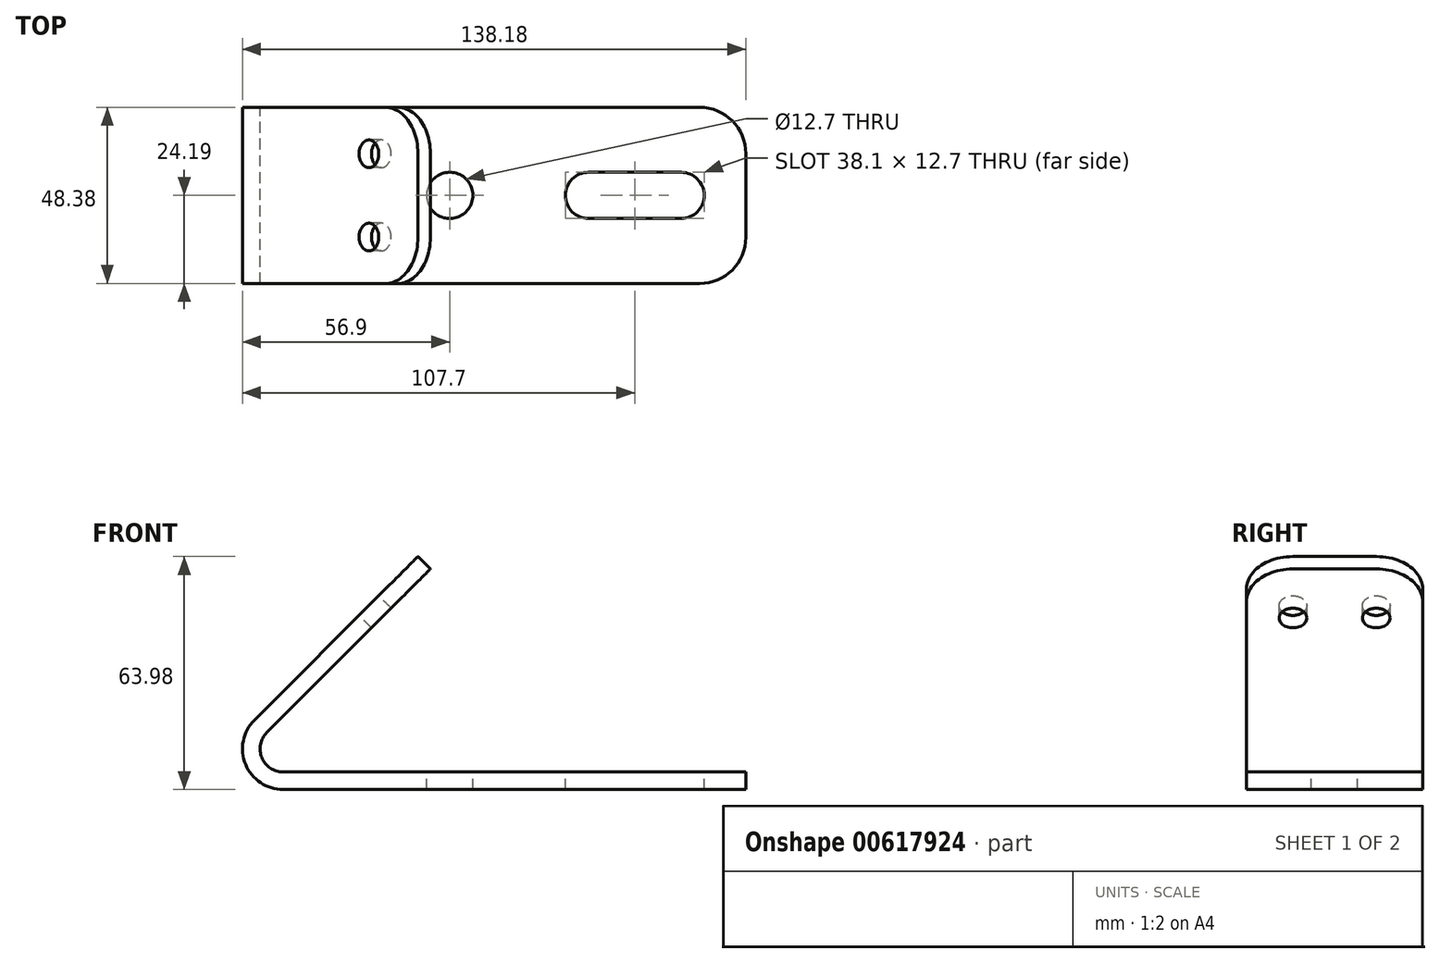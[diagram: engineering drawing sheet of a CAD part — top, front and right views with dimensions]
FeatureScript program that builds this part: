
annotation { "Feature Type Name" : "Feature", "Feature Type Description" : "" }
export const myFeature = defineFeature(function(context is Context, id is Id, definition is map)
    precondition{}
    {
        {
            var Q0;
            Q0=qCreatedBy(makeId("Front.planeOp"),FACE);
            var sketch = newSketch(context, id + "F0", { "sketchPlane" : qUnion([Q0])});
            skLineSegment(sketch, "E0", {"start": v(-8.72, 63.98) * mm, "end": v(-53.62, 19.08) * mm});
            skLineSegment(sketch, "E1", {"start": v(-45.72, 0) * mm, "end": v(81.28, 0) * mm});
            skLineSegment(sketch, "E2", {"start": v(81.28, 0) * mm, "end": v(81.28, 4.83) * mm});
            skLineSegment(sketch, "E3", {"start": v(81.28, 4.83) * mm, "end": v(-45.72, 4.83) * mm});
            skLineSegment(sketch, "E4", {"start": v(-5.3, 60.57) * mm, "end": v(-8.72, 63.98) * mm});
            skPoint(sketch, "E5.visualSharp", {"position": v(-72.7, 0) * mm});
            skArc(sketch, "E5.filletArc", {"start": v(-53.62, 19.08) * mm, "mid": v(-56.05, 6.9) * mm, "end": v(-45.72, 0) * mm});
            skArc(sketch, "E6", {"start": v(-50.21, 15.67) * mm, "mid": v(-51.59, 8.75) * mm, "end": v(-45.72, 4.83) * mm});
            skLineSegment(sketch, "E7.trimOffspring", {"start": v(-50.21, 15.67) * mm, "end": v(-5.3, 60.57) * mm});
            skSolve(sketch);
        }
        {
            var Q0;
            Q0=qSketchRegion(id+"F0",true);
            extrude(context, id + "F1", {"entities" : qUnion([Q0]), "endBound" : BoundingType.SYMMETRIC, "depth" : 48.4 * mm});
        }
        {
            var Q0;
            Q0=makeQuery(id+"F1.opExtrude","SWEPT_FACE",FACE,{"disambiguationData":[OSD([sQuery(id+"F0.wireOp",EDGE,"E0")])]});
            var sketch = newSketch(context, id + "F2", { "sketchPlane" : qUnion([Q0])});
            skCircle(sketch, "E8", {"center": v(-11.43, 20.02) * mm, "radius": 3.81 * mm});
            skCircle(sketch, "E9", {"center": v(11.43, 20.02) * mm, "radius": 3.81 * mm});
            skSolve(sketch);
        }
        {
            var Q0;
            Q0=qSketchRegion(id+"F2",true);
            var Q1;
            Q1=makeQuery(id+"F1.opExtrude","SWEPT_FACE",FACE,{"disambiguationData":[OSD([sQuery(id+"F0.wireOp",EDGE,"E7.trimOffspring")])]});
            extrude(context, id + "F3", {"entities" : qUnion([Q0]), "operationType" : NewBodyOperationType.REMOVE, "endBound" : BoundingType.UP_TO_SURFACE, "oppositeDirection" : true, "endBoundEntityFace" : qUnion([Q1]), "depth" : 25.4 * mm});
        }
        {
            var Q0;
            Q0=makeQuery(id+"F1.opExtrude","SWEPT_FACE",FACE,{"disambiguationData":[OSD([sQuery(id+"F0.wireOp",EDGE,"E3")])]});
            var sketch = newSketch(context, id + "F4", { "sketchPlane" : qUnion([Q0])});
            skCircle(sketch, "E10", {"center": v(0, 0) * mm, "radius": 6.35 * mm});
            skArc(sketch, "E11", {"start": v(38.1, 6.35) * mm, "mid": v(31.75, 0) * mm, "end": v(38.1, -6.35) * mm});
            skArc(sketch, "E12", {"start": v(63.5, -6.35) * mm, "mid": v(69.85, 0) * mm, "end": v(63.5, 6.35) * mm});
            skLineSegment(sketch, "E13", {"start": v(38.1, -6.35) * mm, "end": v(63.5, -6.35) * mm});
            skLineSegment(sketch, "E14", {"start": v(63.5, 6.35) * mm, "end": v(38.1, 6.35) * mm});
            skSolve(sketch);
        }
        {
            var Q0;
            Q0=qSketchRegion(id+"F4",true);
            extrude(context, id + "F5", {"entities" : qUnion([Q0]), "operationType" : NewBodyOperationType.REMOVE, "endBound" : BoundingType.UP_TO_NEXT, "oppositeDirection" : true, "depth" : 25.4 * mm});
        }
        {
            var Q0;
            Q0=makeQuery(id+"F1.opExtrude","CAP_EDGE",EDGE,{"disambiguationData":[OSD([sQuery(id+"F0.wireOp",EDGE,"E4")])],"isStart":false});
            var Q1;
            Q1=makeQuery(id+"F1.opExtrude","CAP_EDGE",EDGE,{"disambiguationData":[OSD([sQuery(id+"F0.wireOp",EDGE,"E4")])],"isStart":true});
            var Q2;
            Q2=makeQuery(id+"F1.opExtrude","CAP_EDGE",EDGE,{"disambiguationData":[OSD([sQuery(id+"F0.wireOp",EDGE,"E2")])],"isStart":true});
            var Q3;
            Q3=makeQuery(id+"F1.opExtrude","CAP_EDGE",EDGE,{"disambiguationData":[OSD([sQuery(id+"F0.wireOp",EDGE,"E2")])],"isStart":false});
            fillet(context, id + "F6", {"entities" : qUnion([Q0, Q1, Q2, Q3]), "radius" : 12.7 * mm, "tangentPropagation" : true, "allowEdgeOverflow" : false});
        }
    });
